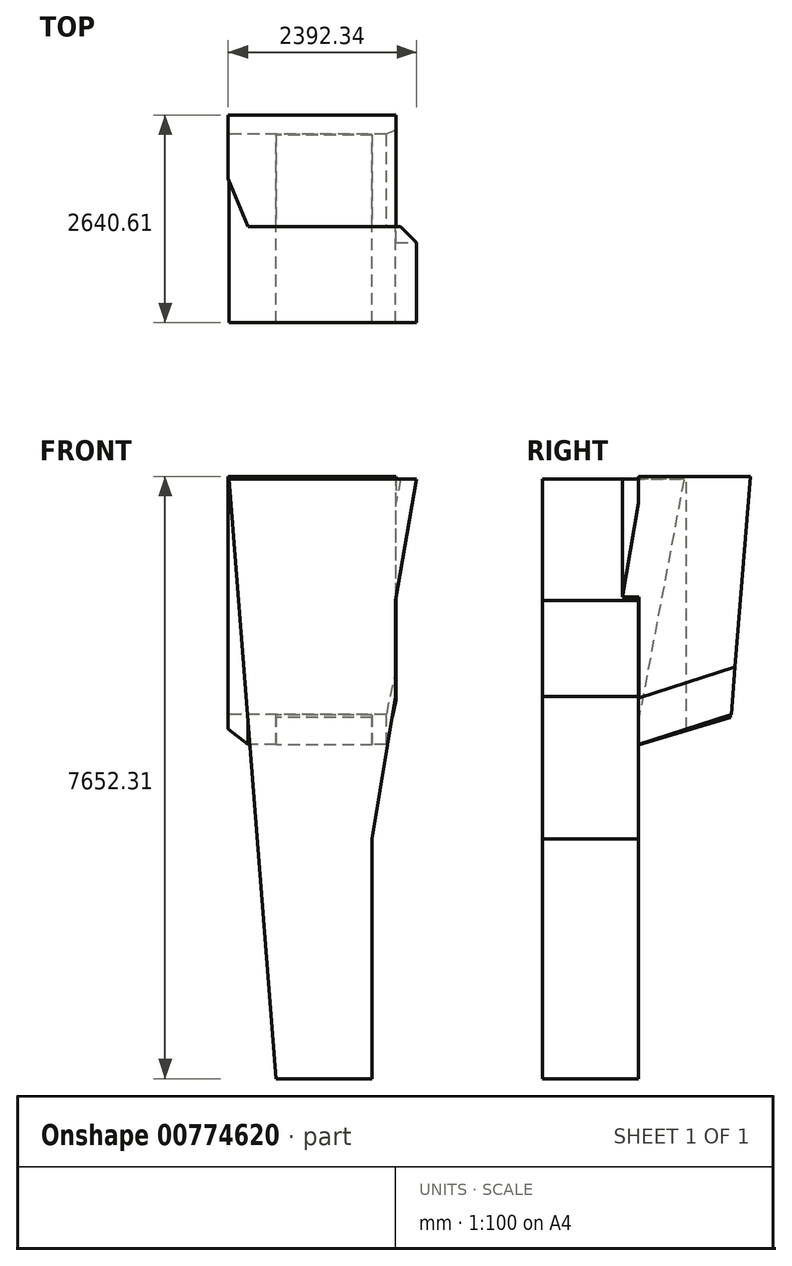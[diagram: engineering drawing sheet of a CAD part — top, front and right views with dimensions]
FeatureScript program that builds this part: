
annotation { "Feature Type Name" : "Feature", "Feature Type Description" : "" }
export const myFeature = defineFeature(function(context is Context, id is Id, definition is map)
    precondition{}
    {
        {
            var Q0;
            Q0=qCreatedBy(makeId("Front.planeOp"),FACE);
            var sketch = newSketch(context, id + "F0", { "sketchPlane" : qUnion([Q0])});
            skLineSegment(sketch, "E0", {"start": v(0, 0) * mm, "end": v(1219.2, 0) * mm});
            skLineSegment(sketch, "E1", {"start": v(1219.2, 0) * mm, "end": v(1219.2, 7620) * mm});
            skLineSegment(sketch, "E2", {"start": v(1219.2, 7620) * mm, "end": v(0, 7620) * mm});
            skLineSegment(sketch, "E3", {"start": v(0, 7620) * mm, "end": v(0, 0) * mm});
            skLineSegment(sketch, "E4", {"start": v(1219.2, 0) * mm, "end": v(1219.2, 3048) * mm});
            skLineSegment(sketch, "E5", {"start": v(1219.2, 3048) * mm, "end": v(1515.47, 4852.64) * mm});
            skLineSegment(sketch, "E6", {"start": v(1515.47, 4852.64) * mm, "end": v(1515.47, 6071.84) * mm});
            skLineSegment(sketch, "E7", {"start": v(1515.47, 6071.84) * mm, "end": v(1782.74, 7620) * mm});
            skLineSegment(sketch, "E8", {"start": v(1782.74, 7620) * mm, "end": v(1219.2, 7620) * mm});
            skLineSegment(sketch, "E9", {"start": v(0, 0) * mm, "end": v(-599.23, 7620) * mm});
            skLineSegment(sketch, "E10", {"start": v(-599.23, 7620) * mm, "end": v(0, 7620) * mm});
            skSolve(sketch);
        }
        {
            var Q0;
            Q0 = qSketchRegion(id + "F0", true);
            extrude(context, id + "F1", {"entities" : qUnion([Q0]), "depth" : 1219.2 * mm, "offsetDistance" : 25.4 * mm});
        }
        {
            var Q0;
            Q0=qCreatedBy(makeId("Right.planeOp"),FACE);
            var sketch = newSketch(context, id + "F2", { "sketchPlane" : qUnion([Q0])});
            skLineSegment(sketch, "E11", {"start": v(0, 0) * mm, "end": v(0, 7620) * mm});
            skLineSegment(sketch, "E12", {"start": v(0, 7620) * mm, "end": v(-1215.54, 7620) * mm});
            skLineSegment(sketch, "E13", {"start": v(-1215.54, 7620) * mm, "end": v(-1215.54, 0) * mm});
            skLineSegment(sketch, "E14", {"start": v(-1215.54, 0) * mm, "end": v(0, 0) * mm});
            skLineSegment(sketch, "E15", {"start": v(0, 4239.68) * mm, "end": v(1167.43, 4591.19) * mm});
            skLineSegment(sketch, "E16", {"start": v(1167.43, 4591.19) * mm, "end": v(1414.86, 7629.36) * mm});
            skLineSegment(sketch, "E17", {"start": v(1414.86, 7629.36) * mm, "end": v(0, 7620) * mm});
            skSolve(sketch);
        }
        {
            var Q0;
            Q0 = qSketchRegion(id + "F2", true);
            extrude(context, id + "F3", {"entities" : qUnion([Q0]), "operationType" : NewBodyOperationType.ADD, "depth" : 1219.2 * mm, "offsetDistance" : 25.4 * mm, "hasSecondDirection" : true, "secondDirectionOppositeDirection" : true, "secondDirectionDepth" : 0 * mm});
        }
        {
            var Q0;
            Q0=qCreatedBy(makeId("Right.planeOp"),FACE);
            var sketch = newSketch(context, id + "F4", { "sketchPlane" : qUnion([Q0])});
            skLineSegment(sketch, "E18", {"start": v(0, 4244.93) * mm, "end": v(1177.06, 4625.03) * mm});
            skLineSegment(sketch, "E19", {"start": v(1177.06, 4625.03) * mm, "end": v(1421.41, 7652.31) * mm});
            skLineSegment(sketch, "E20", {"start": v(1421.41, 7652.31) * mm, "end": v(0, 7652.31) * mm});
            skLineSegment(sketch, "E21", {"start": v(0, 7652.31) * mm, "end": v(0, 4244.93) * mm});
            skSolve(sketch);
        }
        {
            var Q0;
            Q0 = qSketchRegion(id + "F4", true);
            extrude(context, id + "F5", {"entities" : qUnion([Q0]), "operationType" : NewBodyOperationType.ADD, "depth" : 1524 * mm, "offsetDistance" : 25.4 * mm, "hasSecondDirection" : true, "secondDirectionOppositeDirection" : true, "secondDirectionDepth" : 609.6 * mm});
        }
        {
            var Q0;
            Q0=makeQuery(id+"F5.opExtrude","CAP_EDGE",EDGE,{"disambiguationData":[OSD([sQuery(id+"F4.wireOp",EDGE,"E21")])],"isStart":true});
            chamfer(context, id + "F6", {"entities" : qUnion([Q0]), "chamferType" : ChamferType.TWO_OFFSETS, "width1" : 254 * mm, "oppositeDirection" : false, "width2" : 609.6 * mm, "tangentPropagation" : true});
        }
        {
            var Q0;
            {var subQ0=sQuery(id+"F4.wireOp",EDGE,"E21");var subQ1=sQuery(id+"F4.wireOp",EDGE,"E18");var subQ2=makeQuery(id+"F5.opExtrude","CAP_FACE",FACE,{"disambiguationData":[OSD([subQ1,sQuery(id+"F4.wireOp",EDGE,"E19"),sQuery(id+"F4.wireOp",EDGE,"E20"),subQ0])],"isStart":false});var subQ3=sQuery(id+"F0.wireOp",EDGE,"E7");var subQ4=makeQuery(id+"F5.opExtrude","SWEPT_FACE",FACE,{"disambiguationData":[OSD([subQ0])]});Q0=makeQuery(id+"F5.boolean.opBoolean","SPLIT",EDGE,{"disambiguationData":[topologyDisambiguationEdgeConnected([subQ2,subQ4]),TD([makeQuery(id+"F1.opExtrude","SWEPT_FACE",FACE,{"disambiguationData":[OSD([subQ3])]})])],"derivedFrom":makeQuery(id+"F5.opExtrude","CAP_EDGE",EDGE,{"disambiguationData":[OSD([subQ0])],"isStart":false})});}
            chamfer(context, id + "F7", {"entities" : qUnion([Q0]), "width" : 5.08 * mm, "tangentPropagation" : true});
        }
        {
            var Q0;
            Q0=makeQuery(id+"F5.opExtrude","CAP_EDGE",EDGE,{"disambiguationData":[OSD([sQuery(id+"F4.wireOp",EDGE,"E18")])],"isStart":false});
            chamfer(context, id + "F8", {"entities" : qUnion([Q0]), "chamferType" : ChamferType.TWO_OFFSETS, "width1" : 558.8 * mm, "oppositeDirection" : false, "width2" : 127 * mm, "tangentPropagation" : true});
        }
        {
            var Q0;
            {var subQ0=sQuery(id+"F0.wireOp",EDGE,"E7");Q0=makeQuery(id+"F5.boolean.opBoolean","SPLIT",EDGE,{"disambiguationData":[topologyDisambiguationEdgeConnected([makeQuery(id+"F1.opExtrude","CAP_FACE",FACE,{"disambiguationData":[OSD([sQuery(id+"F0.wireOp",EDGE,"E0"),sQuery(id+"F0.wireOp",EDGE,"E2"),sQuery(id+"F0.wireOp",EDGE,"E4"),sQuery(id+"F0.wireOp",EDGE,"E5"),sQuery(id+"F0.wireOp",EDGE,"E6"),subQ0,sQuery(id+"F0.wireOp",EDGE,"E8"),sQuery(id+"F0.wireOp",EDGE,"E9"),sQuery(id+"F0.wireOp",EDGE,"E10")])],"isStart":true})])],"derivedFrom":makeQuery(id+"F1.opExtrude","CAP_EDGE",EDGE,{"disambiguationData":[OSD([subQ0])],"isStart":true})});}
            chamfer(context, id + "F9", {"entities" : qUnion([Q0]), "chamferType" : ChamferType.TWO_OFFSETS, "width1" : 203.2 * mm, "oppositeDirection" : false, "width2" : 203.2 * mm, "tangentPropagation" : true});
        }
    });
